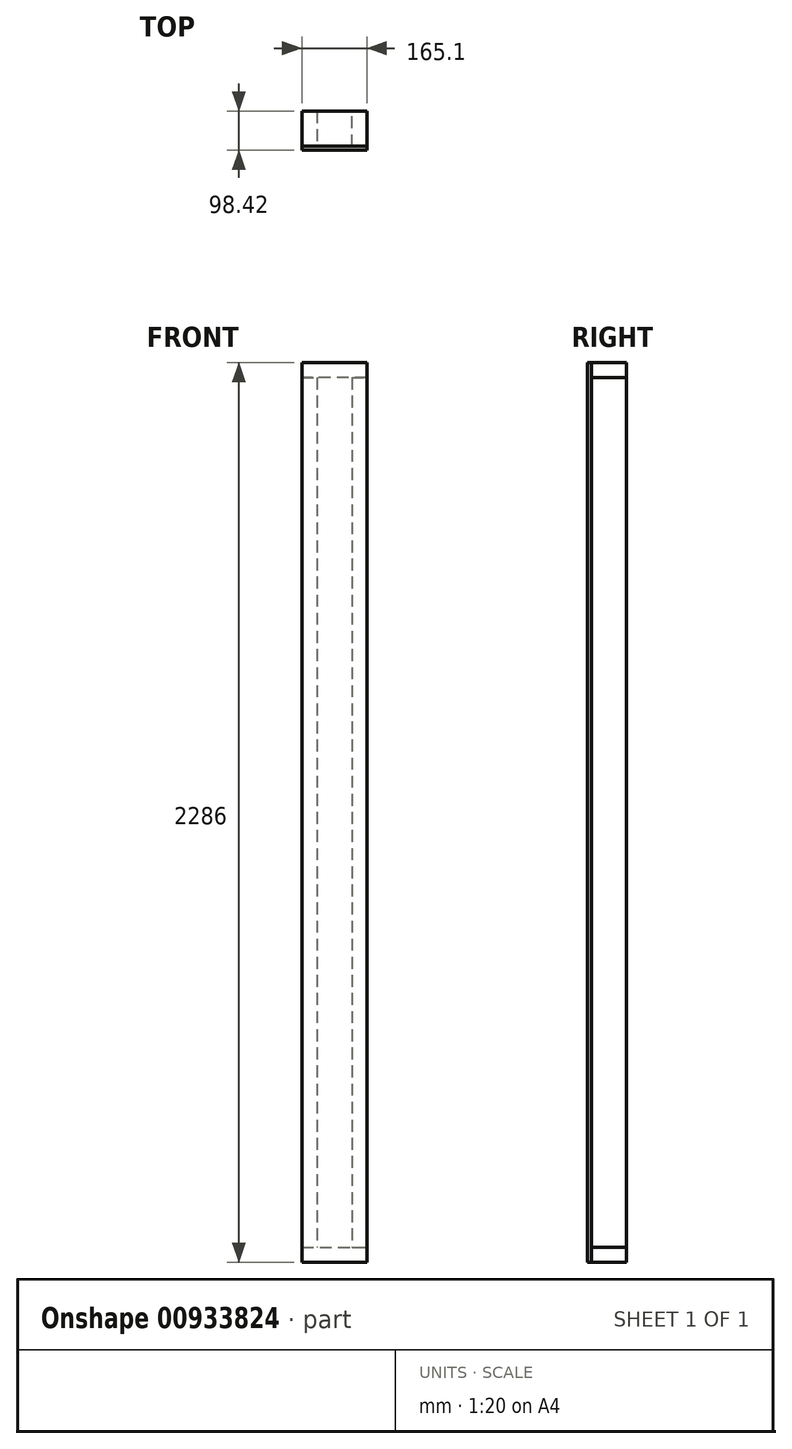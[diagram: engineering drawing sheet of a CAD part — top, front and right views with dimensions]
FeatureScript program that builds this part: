
annotation { "Feature Type Name" : "Feature", "Feature Type Description" : "" }
export const myFeature = defineFeature(function(context is Context, id is Id, definition is map)
    precondition{}
    {
        {
            var Q0;
            Q0=qCreatedBy(makeId("Top.planeOp"),FACE);
            var sketch = newSketch(context, id + "F0", { "sketchPlane" : qUnion([Q0])});
            skLineSegment(sketch, "E0.bottom", {"start": v(0, 0) * mm, "end": v(165.1, 0) * mm});
            skLineSegment(sketch, "E0.top", {"start": v(0, -88.9) * mm, "end": v(165.1, -88.9) * mm});
            skLineSegment(sketch, "E0.left", {"start": v(0, 0) * mm, "end": v(0, -88.9) * mm});
            skLineSegment(sketch, "E0.right", {"start": v(165.1, 0) * mm, "end": v(165.1, -88.9) * mm});
            skSolve(sketch);
        }
        {
            var Q0;
            Q0 = qSketchRegion(id + "F0", true);
            extrude(context, id + "F1", {"entities" : qUnion([Q0]), "depth" : 38.1 * mm, "offsetDistance" : 25.4 * mm});
        }
        {
            var Q0;
            Q0=makeQuery(id+"F1.opExtrude","CAP_FACE",FACE,{"disambiguationData":[OSD([sQuery(id+"F0.wireOp",EDGE,"E0.bottom"),sQuery(id+"F0.wireOp",EDGE,"E0.top"),sQuery(id+"F0.wireOp",EDGE,"E0.left"),sQuery(id+"F0.wireOp",EDGE,"E0.right")])],"isStart":false});
            var sketch = newSketch(context, id + "F2", { "sketchPlane" : qUnion([Q0])});
            skLineSegment(sketch, "E1.bottom", {"start": v(0, 0) * mm, "end": v(38.1, 0) * mm});
            skLineSegment(sketch, "E1.top", {"start": v(0, -88.9) * mm, "end": v(38.1, -88.9) * mm});
            skLineSegment(sketch, "E1.left", {"start": v(0, 0) * mm, "end": v(0, -88.9) * mm});
            skLineSegment(sketch, "E1.right", {"start": v(38.1, 0) * mm, "end": v(38.1, -88.9) * mm});
            skLineSegment(sketch, "E2.bottom", {"start": v(165.1, -88.9) * mm, "end": v(127, -88.9) * mm});
            skLineSegment(sketch, "E2.top", {"start": v(165.1, 0) * mm, "end": v(127, 0) * mm});
            skLineSegment(sketch, "E2.left", {"start": v(165.1, -88.9) * mm, "end": v(165.1, 0) * mm});
            skLineSegment(sketch, "E2.right", {"start": v(127, -88.9) * mm, "end": v(127, 0) * mm});
            skSolve(sketch);
        }
        {
            var Q0;
            Q0 = qSketchRegion(id + "F2", true);
            extrude(context, id + "F3", {"entities" : qUnion([Q0]), "depth" : 2209.8 * mm, "offsetDistance" : 25.4 * mm});
        }
        {
            var Q0;
            Q0=makeQuery(id+"F3.opExtrude","CAP_FACE",FACE,{"disambiguationData":[OSD([sQuery(id+"F2.wireOp",EDGE,"E2.bottom"),sQuery(id+"F2.wireOp",EDGE,"E2.top"),sQuery(id+"F2.wireOp",EDGE,"E2.left"),sQuery(id+"F2.wireOp",EDGE,"E2.right")])],"isStart":false});
            var sketch = newSketch(context, id + "F4", { "sketchPlane" : qUnion([Q0])});
            skLineSegment(sketch, "E3.bottom", {"start": v(165.1, -88.9) * mm, "end": v(0, -88.9) * mm});
            skLineSegment(sketch, "E3.top", {"start": v(165.1, 0) * mm, "end": v(0, 0) * mm});
            skLineSegment(sketch, "E3.left", {"start": v(165.1, -88.9) * mm, "end": v(165.1, 0) * mm});
            skLineSegment(sketch, "E3.right", {"start": v(0, -88.9) * mm, "end": v(0, 0) * mm});
            skSolve(sketch);
        }
        {
            var Q0;
            Q0 = qSketchRegion(id + "F4", true);
            extrude(context, id + "F5", {"entities" : qUnion([Q0]), "depth" : 38.1 * mm, "offsetDistance" : 25.4 * mm});
        }
        {
            var Q0;
            Q0=makeQuery(id+"F5.opExtrude","SWEPT_FACE",FACE,{"disambiguationData":[OSD([sQuery(id+"F4.wireOp",EDGE,"E3.bottom")])]});
            var sketch = newSketch(context, id + "F6", { "sketchPlane" : qUnion([Q0])});
            skLineSegment(sketch, "E4.bottom", {"start": v(165.1, 2286) * mm, "end": v(0, 2286) * mm});
            skLineSegment(sketch, "E4.top", {"start": v(165.1, 0) * mm, "end": v(0, 0) * mm});
            skLineSegment(sketch, "E4.left", {"start": v(165.1, 2286) * mm, "end": v(165.1, 0) * mm});
            skLineSegment(sketch, "E4.right", {"start": v(0, 2286) * mm, "end": v(0, 0) * mm});
            skSolve(sketch);
        }
        {
            var Q0;
            Q0 = qSketchRegion(id + "F6", true);
            extrude(context, id + "F7", {"entities" : qUnion([Q0]), "depth" : 9.52 * mm, "offsetDistance" : 25.4 * mm});
        }
    });
